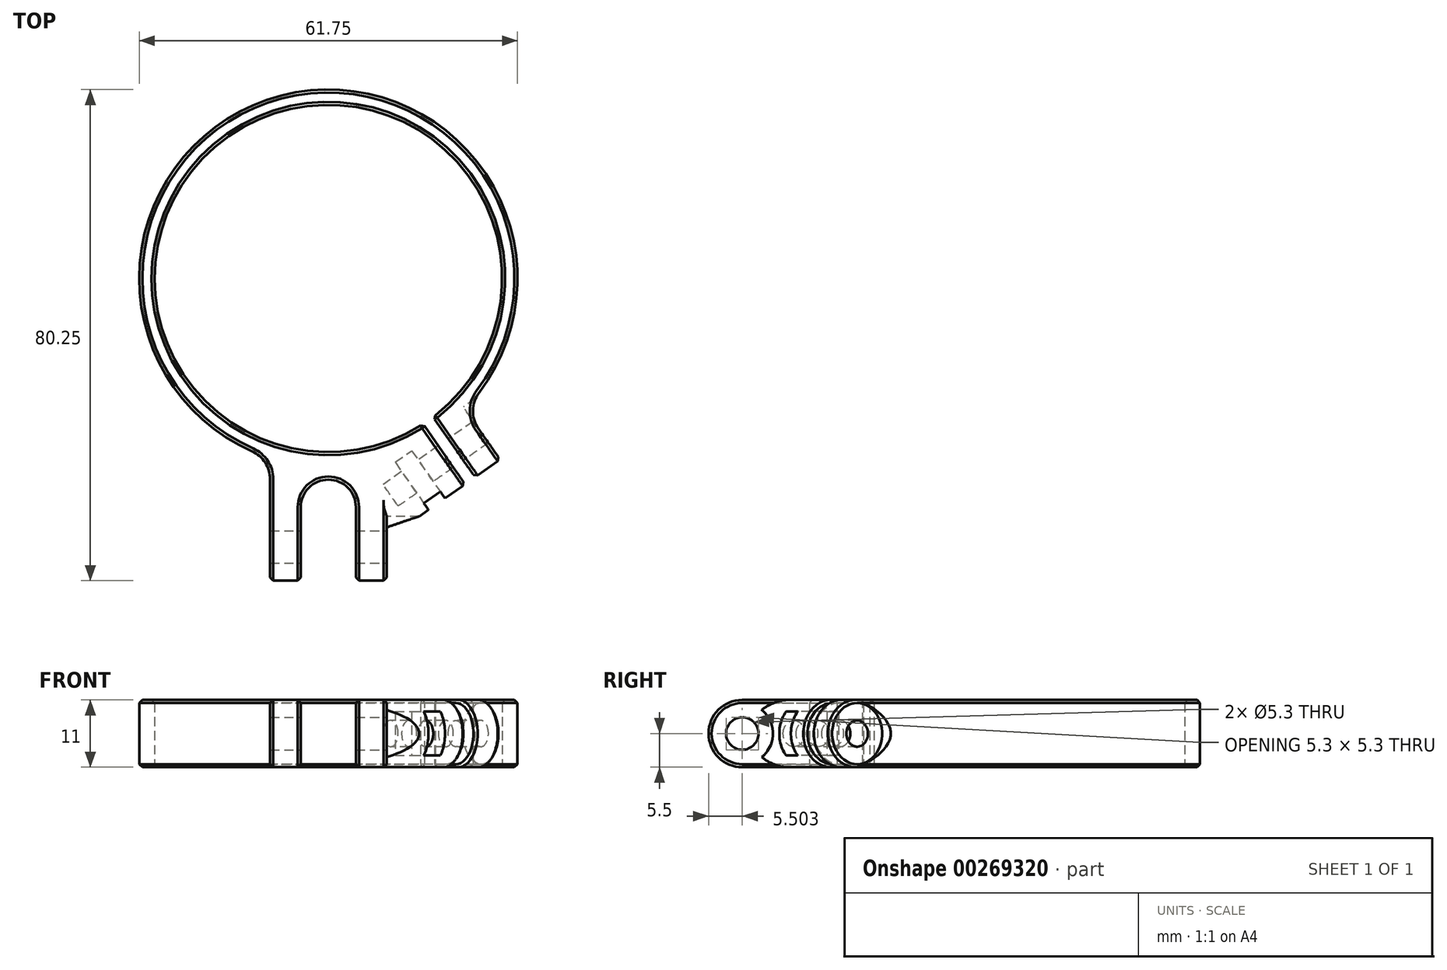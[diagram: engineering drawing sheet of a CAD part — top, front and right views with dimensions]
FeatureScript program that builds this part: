
annotation { "Feature Type Name" : "Feature", "Feature Type Description" : "" }
export const myFeature = defineFeature(function(context is Context, id is Id, definition is map)
    precondition{}
    {
        {
            var Q0;
            Q0=qCreatedBy(makeId("Top.planeOp"),FACE);
            var sketch = newSketch(context, id + "F0", { "sketchPlane" : qUnion([Q0])});
            skLineSegment(sketch, "E0.MirrorCS", {"start": v(-9.5, -29.38) * mm, "end": v(-9.5, -49.38) * mm});
            skLineSegment(sketch, "E1.MirrorCS", {"start": v(-9.5, -49.38) * mm, "end": v(-4.5, -49.38) * mm});
            skLineSegment(sketch, "E2.MirrorCS", {"start": v(-4.5, -49.38) * mm, "end": v(-4.5, -37.38) * mm});
            skArc(sketch, "E3.MirrorCS", {"start": v(-4.5, -37.38) * mm, "mid": v(0, -32.88) * mm, "end": v(4.5, -37.38) * mm});
            skLineSegment(sketch, "E4.MirrorCS", {"start": v(4.5, -37.38) * mm, "end": v(4.5, -49.38) * mm});
            skLineSegment(sketch, "E5.MirrorCS", {"start": v(4.5, -49.38) * mm, "end": v(9.5, -49.38) * mm});
            skLineSegment(sketch, "E6.MirrorCS", {"start": v(9.5, -49.38) * mm, "end": v(9.5, -42.62) * mm});
            skLineSegment(sketch, "E7.MirrorCS", {"start": v(22.33, -33.63) * mm, "end": v(9.5, -42.62) * mm});
            skLineSegment(sketch, "E8.MirrorCS", {"start": v(22.33, -33.63) * mm, "end": v(15.45, -23.8) * mm});
            skLineSegment(sketch, "E9.MirrorCS", {"start": v(17.08, -22.66) * mm, "end": v(23.97, -32.49) * mm});
            skLineSegment(sketch, "E10.MirrorCS", {"start": v(23.97, -32.49) * mm, "end": v(28.06, -29.62) * mm});
            skLineSegment(sketch, "E11.MirrorCS", {"start": v(28.06, -29.62) * mm, "end": v(22.29, -21.37) * mm});
            skArc(sketch, "E12", {"start": v(22.29, -21.37) * mm, "mid": v(-7.54, 29.94) * mm, "end": v(-9.5, -29.38) * mm});
            skArc(sketch, "E13", {"start": v(17.08, -22.66) * mm, "mid": v(-16.28, 23.24) * mm, "end": v(15.45, -23.8) * mm});
            skLineSegment(sketch, "E14", {"start": v(0, 0) * mm, "end": v(34.57, -49.38) * mm, "construction": true});
            skLineSegment(sketch, "E15", {"start": v(0, 0) * mm, "end": v(0, -37.38) * mm, "construction": true});
            skSolve(sketch);
        }
        {
            var Q0;
            Q0=qSketchRegion(id+"F0",true);
            extrude(context, id + "F1", {"entities" : qUnion([Q0]), "endBound" : BoundingType.SYMMETRIC, "depth" : 11 * mm});
        }
        {
            var Q0;
            Q0=makeQuery(id+"F1.opExtrude","SWEPT_FACE",FACE,{"disambiguationData":[OSD([sQuery(id+"F0.wireOp",EDGE,"E7.MirrorCS")])]});
            var sketch = newSketch(context, id + "F2", { "sketchPlane" : qUnion([Q0])});
            skLineSegment(sketch, "E16", {"start": v(-1, 0) * mm, "end": v(-16.66, 0) * mm, "construction": true});
            skLineSegment(sketch, "E17.bottom", {"start": v(-8.3, 3.6) * mm, "end": v(-5, 3.6) * mm});
            skLineSegment(sketch, "E17.top", {"start": v(-8.3, -3.6) * mm, "end": v(-5, -3.6) * mm});
            skLineSegment(sketch, "E17.left", {"start": v(-8.3, 3.6) * mm, "end": v(-8.3, -3.6) * mm});
            skLineSegment(sketch, "E17.right", {"start": v(-5, 3.6) * mm, "end": v(-5, -3.6) * mm});
            skPoint(sketch, "E17.middle", {"position": v(-6.65, 0) * mm});
            skSolve(sketch);
        }
        {
            var Q0;
            Q0=qSketchRegion(id+"F2",true);
            extrude(context, id + "F3", {"entities" : qUnion([Q0]), "operationType" : NewBodyOperationType.REMOVE, "oppositeDirection" : true, "depth" : 9.5 * mm});
        }
        {
            var Q0;
            Q0=makeQuery(id+"F1.opExtrude","SWEPT_EDGE",EDGE,{"disambiguationData":[OSD([sQuery(id+"F0.wireOp",EDGE,"E0.MirrorCS"),sQuery(id+"F0.wireOp",EDGE,"E12")])]});
            var Q1;
            Q1=makeQuery(id+"F1.opExtrude","SWEPT_EDGE",EDGE,{"disambiguationData":[OSD([sQuery(id+"F0.wireOp",EDGE,"E11.MirrorCS"),sQuery(id+"F0.wireOp",EDGE,"E12")])]});
            fillet(context, id + "F4", {"entities" : qUnion([Q0, Q1]), "radius" : 5 * mm, "tangentPropagation" : true, "allowEdgeOverflow" : false});
        }
        {
            var Q0;
            Q0=makeQuery(id+"F1.opExtrude","CAP_EDGE",EDGE,{"disambiguationData":[OSD([sQuery(id+"F0.wireOp",EDGE,"E10.MirrorCS")])],"isStart":false});
            var Q1;
            Q1=makeQuery(id+"F1.opExtrude","CAP_EDGE",EDGE,{"disambiguationData":[OSD([sQuery(id+"F0.wireOp",EDGE,"E10.MirrorCS")])],"isStart":true});
            var Q2;
            Q2=makeQuery(id+"F1.opExtrude","CAP_EDGE",EDGE,{"disambiguationData":[OSD([sQuery(id+"F0.wireOp",EDGE,"E7.MirrorCS")])],"isStart":false});
            var Q3;
            Q3=makeQuery(id+"F1.opExtrude","CAP_EDGE",EDGE,{"disambiguationData":[OSD([sQuery(id+"F0.wireOp",EDGE,"E7.MirrorCS")])],"isStart":true});
            var Q4;
            Q4=makeQuery(id+"F1.opExtrude","CAP_EDGE",EDGE,{"disambiguationData":[OSD([sQuery(id+"F0.wireOp",EDGE,"E5.MirrorCS")])],"isStart":false});
            var Q5;
            Q5=makeQuery(id+"F1.opExtrude","CAP_EDGE",EDGE,{"disambiguationData":[OSD([sQuery(id+"F0.wireOp",EDGE,"E1.MirrorCS")])],"isStart":false});
            var Q6;
            Q6=makeQuery(id+"F1.opExtrude","CAP_EDGE",EDGE,{"disambiguationData":[OSD([sQuery(id+"F0.wireOp",EDGE,"E5.MirrorCS")])],"isStart":true});
            var Q7;
            Q7=makeQuery(id+"F1.opExtrude","CAP_EDGE",EDGE,{"disambiguationData":[OSD([sQuery(id+"F0.wireOp",EDGE,"E1.MirrorCS")])],"isStart":true});
            fillet(context, id + "F5", {"entities" : qUnion([Q0, Q1, Q2, Q3, Q4, Q5, Q6, Q7]), "radius" : 5.5 * mm, "tangentPropagation" : true, "allowEdgeOverflow" : false});
        }
        {
            var Q0;
            Q0=makeQuery(id+"F1.opExtrude","SWEPT_FACE",FACE,{"disambiguationData":[OSD([sQuery(id+"F0.wireOp",EDGE,"E6.MirrorCS")])]});
            var sketch = newSketch(context, id + "F6", { "sketchPlane" : qUnion([Q0])});
            skCircle(sketch, "E18", {"center": v(-43.88, 0) * mm, "radius": 2.65 * mm});
            skSolve(sketch);
        }
        {
            var Q0;
            Q0=qSketchRegion(id+"F6",true);
            var Q1;
            Q1=makeQuery(id+"F1.opExtrude","SWEPT_FACE",FACE,{"disambiguationData":[OSD([sQuery(id+"F0.wireOp",EDGE,"E0.MirrorCS")])]});
            var Q2;
            Q2=makeQuery(id+"F1.opExtrude","SWEPT_FACE",FACE,{"disambiguationData":[OSD([sQuery(id+"F0.wireOp",EDGE,"E8.MirrorCS")])]});
            extrude(context, id + "F7", {"entities" : qUnion([Q0]), "operationType" : NewBodyOperationType.REMOVE, "endBound" : BoundingType.UP_TO_SURFACE, "oppositeDirection" : true, "endBoundEntityFace" : qUnion([Q1]), "depth" : 50 * mm, "hasSecondDirection" : true, "secondDirectionBound" : SecondDirectionBoundingType.UP_TO_SURFACE, "secondDirectionOppositeDirection" : false, "secondDirectionBoundEntityFace" : qUnion([Q2]), "secondDirectionDepth" : 25 * mm});
        }
        {
            var Q0;
            Q0=makeQuery(id+"F1.opExtrude","SWEPT_FACE",FACE,{"disambiguationData":[OSD([sQuery(id+"F0.wireOp",EDGE,"E6.MirrorCS")])]});
            var sketch = newSketch(context, id + "F8", { "sketchPlane" : qUnion([Q0])});
            skCircle(sketch, "E19", {"center": v(-43.88, 0) * mm, "radius": 5 * mm});
            skSolve(sketch);
        }
        {
            var Q0;
            Q0=qSketchRegion(id+"F8",true);
            var Q1;
            Q1=makeQuery(id+"F1.opExtrude","SWEPT_FACE",FACE,{"disambiguationData":[OSD([sQuery(id+"F0.wireOp",EDGE,"E8.MirrorCS")])]});
            extrude(context, id + "F9", {"entities" : qUnion([Q0]), "operationType" : NewBodyOperationType.REMOVE, "endBound" : BoundingType.UP_TO_SURFACE, "endBoundEntityFace" : qUnion([Q1]), "depth" : 25 * mm});
        }
        {
            var Q0;
            Q0=makeQuery(id+"F1.opExtrude","SWEPT_FACE",FACE,{"disambiguationData":[OSD([sQuery(id+"F0.wireOp",EDGE,"E9.MirrorCS")])]});
            var Q1;
            Q1=makeQuery(id+"F1.opExtrude","SWEPT_FACE",FACE,{"disambiguationData":[OSD([sQuery(id+"F0.wireOp",EDGE,"E8.MirrorCS")])]});
            cPlane(context, id + "F10", {"entities" : qUnion([Q0, Q1]), "cplaneType" : CPlaneType.MID_PLANE, "offset" : 25 * mm, "width" : 150 * mm, "height" : 150 * mm});
        }
        {
            var Q0;
            Q0=qCreatedBy(id+"F10.planeOp",FACE);
            var sketch = newSketch(context, id + "F11", { "sketchPlane" : qUnion([Q0])});
            skCircle(sketch, "E20", {"center": v(34.86, 0) * mm, "radius": 2.15 * mm});
            skSolve(sketch);
        }
        {
            var Q0;
            Q0=qSketchRegion(id+"F11",true);
            var Q1;
            Q1=makeQuery(id+"F1.opExtrude","SWEPT_FACE",FACE,{"disambiguationData":[OSD([sQuery(id+"F0.wireOp",EDGE,"E11.MirrorCS")])]});
            var Q2;
            {var subQ0=sQuery(id+"F0.wireOp",EDGE,"E12");var subQ1=sQuery(id+"F0.wireOp",EDGE,"E11.MirrorCS");Q2=makeQuery(id+"F4.opFillet","BLEND_VERTEX",VERTEX,{"blendedFrom":[makeQuery(id+"F1.opExtrude","SWEPT_EDGE",EDGE,{"disambiguationData":[OSD([subQ1,subQ0])]}),makeQuery(id+"F1.opExtrude","CAP_FACE",FACE,{"disambiguationData":[OSD([sQuery(id+"F0.wireOp",EDGE,"E0.MirrorCS"),sQuery(id+"F0.wireOp",EDGE,"E1.MirrorCS"),sQuery(id+"F0.wireOp",EDGE,"E2.MirrorCS"),sQuery(id+"F0.wireOp",EDGE,"E3.MirrorCS"),sQuery(id+"F0.wireOp",EDGE,"E4.MirrorCS"),sQuery(id+"F0.wireOp",EDGE,"E5.MirrorCS"),sQuery(id+"F0.wireOp",EDGE,"E6.MirrorCS"),sQuery(id+"F0.wireOp",EDGE,"E7.MirrorCS"),sQuery(id+"F0.wireOp",EDGE,"E8.MirrorCS"),sQuery(id+"F0.wireOp",EDGE,"E9.MirrorCS"),sQuery(id+"F0.wireOp",EDGE,"E10.MirrorCS"),subQ1,subQ0,sQuery(id+"F0.wireOp",EDGE,"E13")])],"isStart":true}),makeQuery(id+"F1.opExtrude","SWEPT_FACE",FACE,{"disambiguationData":[OSD([subQ0])]})],"blendedInto":[makeQuery(id+"F1.opExtrude","CAP_FACE",FACE,{"disambiguationData":[OSD([sQuery(id+"F0.wireOp",EDGE,"E0.MirrorCS"),sQuery(id+"F0.wireOp",EDGE,"E1.MirrorCS"),sQuery(id+"F0.wireOp",EDGE,"E2.MirrorCS"),sQuery(id+"F0.wireOp",EDGE,"E3.MirrorCS"),sQuery(id+"F0.wireOp",EDGE,"E4.MirrorCS"),sQuery(id+"F0.wireOp",EDGE,"E5.MirrorCS"),sQuery(id+"F0.wireOp",EDGE,"E6.MirrorCS"),sQuery(id+"F0.wireOp",EDGE,"E7.MirrorCS"),sQuery(id+"F0.wireOp",EDGE,"E8.MirrorCS"),sQuery(id+"F0.wireOp",EDGE,"E9.MirrorCS"),sQuery(id+"F0.wireOp",EDGE,"E10.MirrorCS"),subQ1,subQ0,sQuery(id+"F0.wireOp",EDGE,"E13")])],"isStart":true}),makeQuery(id+"F1.opExtrude","SWEPT_FACE",FACE,{"disambiguationData":[OSD([subQ0])]})]});}
            extrude(context, id + "F12", {"entities" : qUnion([Q0]), "operationType" : NewBodyOperationType.REMOVE, "endBound" : BoundingType.UP_TO_VERTEX, "oppositeDirection" : true, "endBoundEntityFace" : qUnion([Q1]), "endBoundEntityVertex" : qUnion([Q2]), "depth" : 25 * mm, "hasSecondDirection" : true, "secondDirectionOppositeDirection" : false, "secondDirectionDepth" : 12 * mm});
        }
        {
            var Q0;
            Q0=makeQuery(id+"F1.opExtrude","SWEPT_FACE",FACE,{"disambiguationData":[OSD([sQuery(id+"F0.wireOp",EDGE,"E11.MirrorCS")])]});
            var sketch = newSketch(context, id + "F13", { "sketchPlane" : qUnion([Q0])});
            skCircle(sketch, "E21", {"center": v(-34.86, 0) * mm, "radius": 5 * mm});
            skSolve(sketch);
        }
        {
            var Q0;
            Q0=qSketchRegion(id+"F13",true);
            var Q1;
            {var subQ0=sQuery(id+"F0.wireOp",EDGE,"E12");var subQ1=sQuery(id+"F0.wireOp",EDGE,"E11.MirrorCS");Q1=makeQuery(id+"F4.opFillet","BLEND_VERTEX",VERTEX,{"blendedFrom":[makeQuery(id+"F1.opExtrude","SWEPT_EDGE",EDGE,{"disambiguationData":[OSD([subQ1,subQ0])]}),makeQuery(id+"F1.opExtrude","CAP_FACE",FACE,{"disambiguationData":[OSD([sQuery(id+"F0.wireOp",EDGE,"E0.MirrorCS"),sQuery(id+"F0.wireOp",EDGE,"E1.MirrorCS"),sQuery(id+"F0.wireOp",EDGE,"E2.MirrorCS"),sQuery(id+"F0.wireOp",EDGE,"E3.MirrorCS"),sQuery(id+"F0.wireOp",EDGE,"E4.MirrorCS"),sQuery(id+"F0.wireOp",EDGE,"E5.MirrorCS"),sQuery(id+"F0.wireOp",EDGE,"E6.MirrorCS"),sQuery(id+"F0.wireOp",EDGE,"E7.MirrorCS"),sQuery(id+"F0.wireOp",EDGE,"E8.MirrorCS"),sQuery(id+"F0.wireOp",EDGE,"E9.MirrorCS"),sQuery(id+"F0.wireOp",EDGE,"E10.MirrorCS"),subQ1,subQ0,sQuery(id+"F0.wireOp",EDGE,"E13")])],"isStart":true}),makeQuery(id+"F1.opExtrude","SWEPT_FACE",FACE,{"disambiguationData":[OSD([subQ0])]})],"blendedInto":[makeQuery(id+"F1.opExtrude","CAP_FACE",FACE,{"disambiguationData":[OSD([sQuery(id+"F0.wireOp",EDGE,"E0.MirrorCS"),sQuery(id+"F0.wireOp",EDGE,"E1.MirrorCS"),sQuery(id+"F0.wireOp",EDGE,"E2.MirrorCS"),sQuery(id+"F0.wireOp",EDGE,"E3.MirrorCS"),sQuery(id+"F0.wireOp",EDGE,"E4.MirrorCS"),sQuery(id+"F0.wireOp",EDGE,"E5.MirrorCS"),sQuery(id+"F0.wireOp",EDGE,"E6.MirrorCS"),sQuery(id+"F0.wireOp",EDGE,"E7.MirrorCS"),sQuery(id+"F0.wireOp",EDGE,"E8.MirrorCS"),sQuery(id+"F0.wireOp",EDGE,"E9.MirrorCS"),sQuery(id+"F0.wireOp",EDGE,"E10.MirrorCS"),subQ1,subQ0,sQuery(id+"F0.wireOp",EDGE,"E13")])],"isStart":true}),makeQuery(id+"F1.opExtrude","SWEPT_FACE",FACE,{"disambiguationData":[OSD([subQ0])]})]});}
            extrude(context, id + "F14", {"entities" : qUnion([Q0]), "operationType" : NewBodyOperationType.REMOVE, "endBound" : BoundingType.UP_TO_VERTEX, "endBoundEntityVertex" : qUnion([Q1]), "depth" : 25 * mm});
        }
        {
            var Q0;
            Q0=makeQuery(id+"F1.opExtrude","CAP_FACE",FACE,{"disambiguationData":[OSD([sQuery(id+"F0.wireOp",EDGE,"E0.MirrorCS"),sQuery(id+"F0.wireOp",EDGE,"E1.MirrorCS"),sQuery(id+"F0.wireOp",EDGE,"E2.MirrorCS"),sQuery(id+"F0.wireOp",EDGE,"E3.MirrorCS"),sQuery(id+"F0.wireOp",EDGE,"E4.MirrorCS"),sQuery(id+"F0.wireOp",EDGE,"E5.MirrorCS"),sQuery(id+"F0.wireOp",EDGE,"E6.MirrorCS"),sQuery(id+"F0.wireOp",EDGE,"E7.MirrorCS"),sQuery(id+"F0.wireOp",EDGE,"E8.MirrorCS"),sQuery(id+"F0.wireOp",EDGE,"E9.MirrorCS"),sQuery(id+"F0.wireOp",EDGE,"E10.MirrorCS"),sQuery(id+"F0.wireOp",EDGE,"E11.MirrorCS"),sQuery(id+"F0.wireOp",EDGE,"E12"),sQuery(id+"F0.wireOp",EDGE,"E13")])],"isStart":true});
            var Q1;
            Q1=makeQuery(id+"F1.opExtrude","SWEPT_EDGE",EDGE,{"disambiguationData":[OSD([sQuery(id+"F0.wireOp",EDGE,"E8.MirrorCS"),sQuery(id+"F0.wireOp",EDGE,"E13")])]});
            var Q2;
            Q2=makeQuery(id+"F1.opExtrude","SWEPT_EDGE",EDGE,{"disambiguationData":[OSD([sQuery(id+"F0.wireOp",EDGE,"E9.MirrorCS"),sQuery(id+"F0.wireOp",EDGE,"E13")])]});
            var Q3;
            Q3=makeQuery(id+"F1.opExtrude","CAP_FACE",FACE,{"disambiguationData":[OSD([sQuery(id+"F0.wireOp",EDGE,"E0.MirrorCS"),sQuery(id+"F0.wireOp",EDGE,"E1.MirrorCS"),sQuery(id+"F0.wireOp",EDGE,"E2.MirrorCS"),sQuery(id+"F0.wireOp",EDGE,"E3.MirrorCS"),sQuery(id+"F0.wireOp",EDGE,"E4.MirrorCS"),sQuery(id+"F0.wireOp",EDGE,"E5.MirrorCS"),sQuery(id+"F0.wireOp",EDGE,"E6.MirrorCS"),sQuery(id+"F0.wireOp",EDGE,"E7.MirrorCS"),sQuery(id+"F0.wireOp",EDGE,"E8.MirrorCS"),sQuery(id+"F0.wireOp",EDGE,"E9.MirrorCS"),sQuery(id+"F0.wireOp",EDGE,"E10.MirrorCS"),sQuery(id+"F0.wireOp",EDGE,"E11.MirrorCS"),sQuery(id+"F0.wireOp",EDGE,"E12"),sQuery(id+"F0.wireOp",EDGE,"E13")])],"isStart":false});
            chamfer(context, id + "F15", {"entities" : qUnion([Q0, Q1, Q2, Q3]), "width" : 0.5 * mm, "tangentPropagation" : true});
        }
    });
